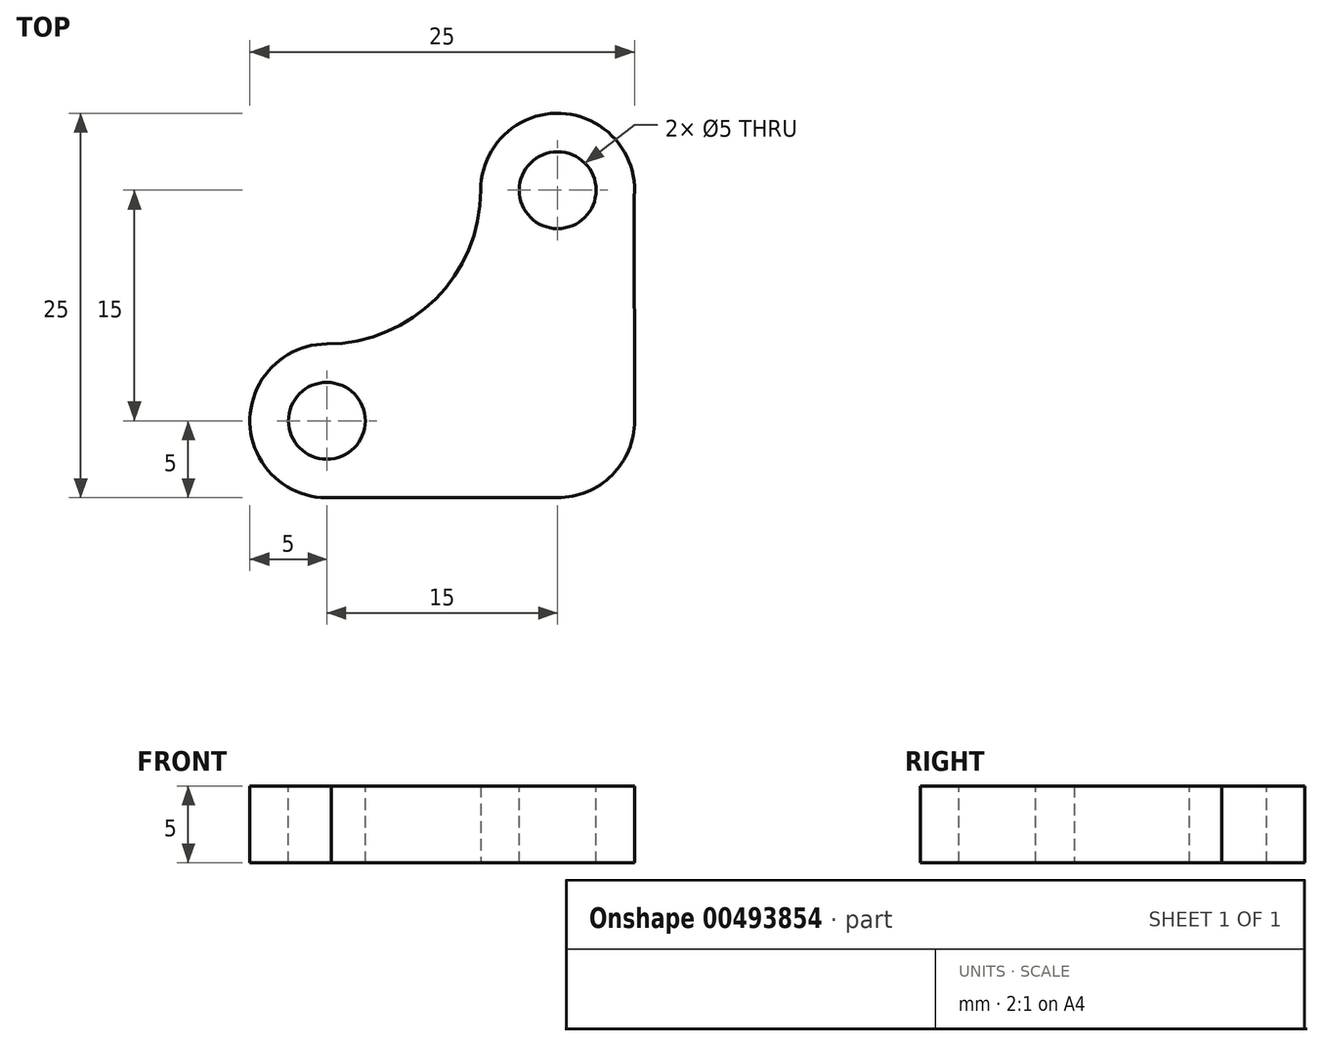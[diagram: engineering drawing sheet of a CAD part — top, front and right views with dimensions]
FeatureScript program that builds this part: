
annotation { "Feature Type Name" : "Feature", "Feature Type Description" : "" }
export const myFeature = defineFeature(function(context is Context, id is Id, definition is map)
    precondition{}
    {
        {
            var Q0;
            Q0=qCreatedBy(makeId("Top.planeOp"),FACE);
            var sketch = newSketch(context, id + "F0", { "sketchPlane" : qUnion([Q0])});
            skArc(sketch, "E0", {"start": v(0, -5) * mm, "mid": v(3.54, -3.53) * mm, "end": v(5, 0) * mm});
            skArc(sketch, "E1", {"start": v(4.98, 14.6) * mm, "mid": v(0.2, 20) * mm, "end": v(-5, 15) * mm});
            skArc(sketch, "E2", {"start": v(-15, 5) * mm, "mid": v(-20, -0.15) * mm, "end": v(-14.7, -5) * mm});
            skArc(sketch, "E3", {"start": v(-15, 5) * mm, "mid": v(-7.93, 7.93) * mm, "end": v(-5, 15) * mm});
            skLineSegment(sketch, "E4", {"start": v(4.98, 15.42) * mm, "end": v(5, 0) * mm});
            skLineSegment(sketch, "E5", {"start": v(-14.7, -5) * mm, "end": v(0, -5) * mm});
            skSolve(sketch);
        }
        {
            var Q0;
            Q0 = qSketchRegion(id + "F0", true);
            extrude(context, id + "F1", {"entities" : qUnion([Q0]), "depth" : 5 * mm});
        }
        {
            var Q0;
            Q0=makeQuery(id+"F1.opExtrude","CAP_FACE",FACE,{"disambiguationData":[OSD([sQuery(id+"F0.wireOp",EDGE,"E0"),sQuery(id+"F0.wireOp",EDGE,"E1"),sQuery(id+"F0.wireOp",EDGE,"E2"),sQuery(id+"F0.wireOp",EDGE,"E3"),sQuery(id+"F0.wireOp",EDGE,"E4"),sQuery(id+"F0.wireOp",EDGE,"E5")])],"isStart":false});
            var sketch = newSketch(context, id + "F2", { "sketchPlane" : qUnion([Q0])});
            skPoint(sketch, "E6", {"position": v(0, 15) * mm});
            skPoint(sketch, "E7", {"position": v(-15, 0) * mm});
            skSolve(sketch);
        }
        {
            var Q0;
            Q0=sQuery(id+"F2.wireOp",VERTEX,"E6");
            var Q1;
            Q1=sQuery(id+"F2.wireOp",VERTEX,"E7");
            var Q2;
            Q2=makeQuery(id+"F1.opExtrude","SWEPT_BODY",BODY,{"disambiguationData":[OSD([sQuery(id+"F0.wireOp",EDGE,"E0"),sQuery(id+"F0.wireOp",EDGE,"E1"),sQuery(id+"F0.wireOp",EDGE,"E2"),sQuery(id+"F0.wireOp",EDGE,"E3"),sQuery(id+"F0.wireOp",EDGE,"E4"),sQuery(id+"F0.wireOp",EDGE,"E5")])]});
            hole(context, id + "F3", {"style" : HoleStyle.SIMPLE, "endStyle" : HoleEndStyle.THROUGH, "holeDiameter" : 5 * mm, "isTappedThrough" : true, "tappedDepth" : 12 * mm, "tapClearance" : 3, "locations" : qUnion([Q0, Q1]), "scope" : qUnion([Q2])});
        }
    });
